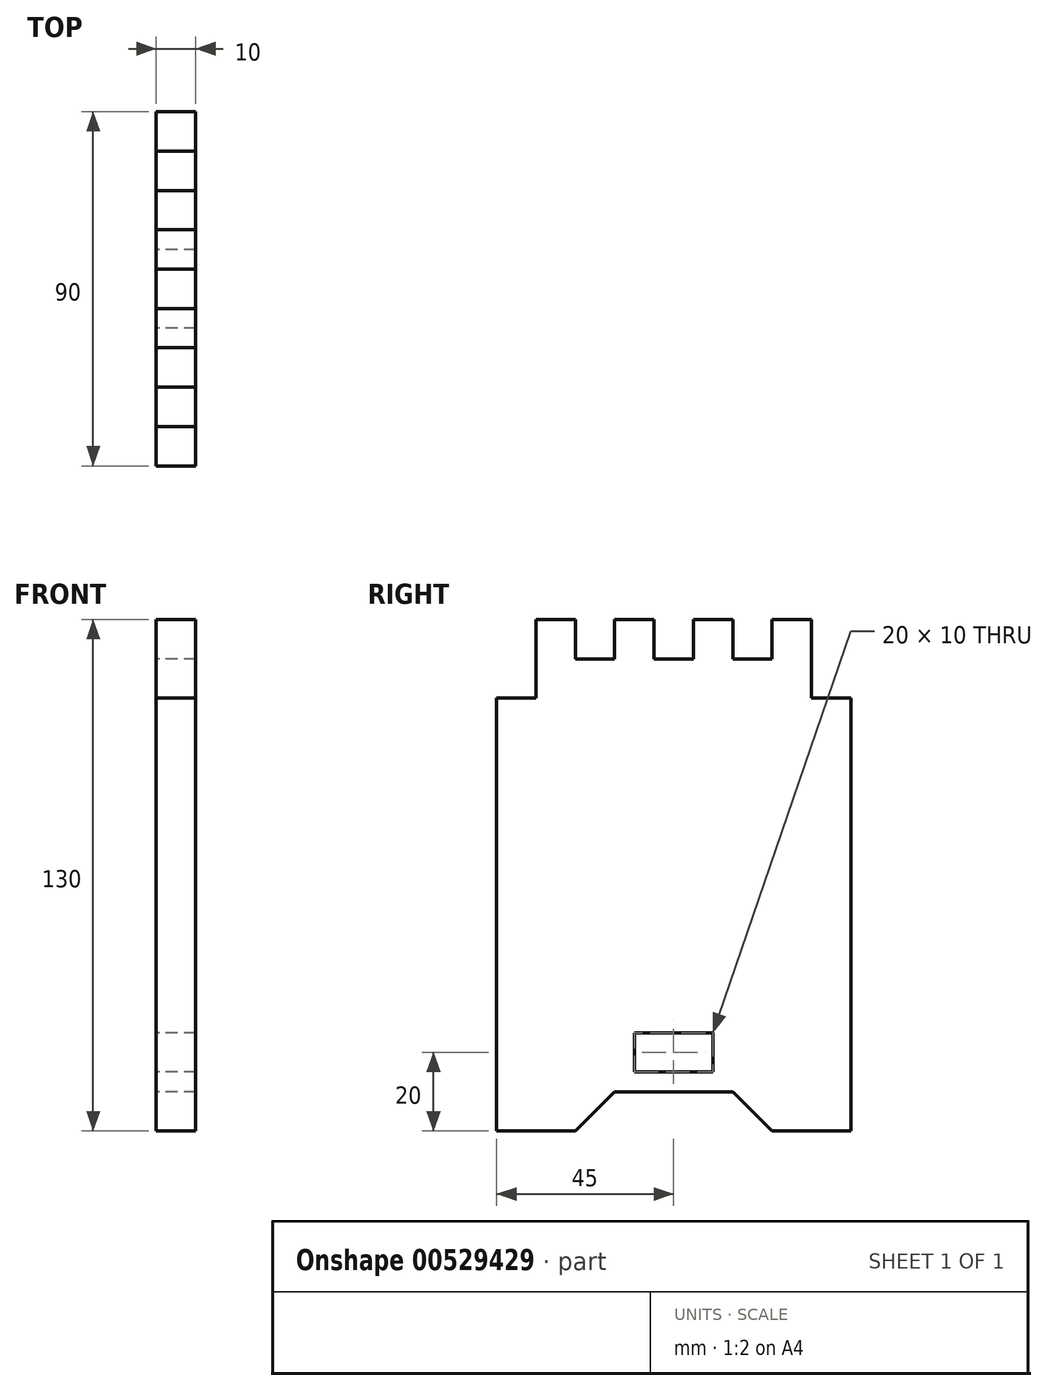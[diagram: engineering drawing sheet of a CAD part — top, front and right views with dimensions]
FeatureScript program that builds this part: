
annotation { "Feature Type Name" : "Feature", "Feature Type Description" : "" }
export const myFeature = defineFeature(function(context is Context, id is Id, definition is map)
    precondition{}
    {
        {
            var Q0;
            Q0=qCreatedBy(makeId("Right.planeOp"),FACE);
            var sketch = newSketch(context, id + "F0", { "sketchPlane" : qUnion([Q0])});
            skLineSegment(sketch, "E0.left", {"start": v(45, -65) * mm, "end": v(45, 45) * mm});
            skLineSegment(sketch, "E0.right", {"start": v(-45, -65) * mm, "end": v(-45, 45) * mm});
            skPoint(sketch, "E0.middle", {"position": v(0, 0) * mm});
            skLineSegment(sketch, "E1", {"start": v(45, -65) * mm, "end": v(25, -65) * mm});
            skLineSegment(sketch, "E2", {"start": v(25, -65) * mm, "end": v(15, -55) * mm});
            skLineSegment(sketch, "E3.MirrorCS", {"start": v(-25, -65) * mm, "end": v(-15, -55) * mm});
            skLineSegment(sketch, "E4.MirrorCS", {"start": v(-45, -65) * mm, "end": v(-25, -65) * mm});
            skLineSegment(sketch, "E5", {"start": v(-15, -55) * mm, "end": v(15, -55) * mm});
            skLineSegment(sketch, "E6", {"start": v(-35, 65) * mm, "end": v(-25, 65) * mm});
            skLineSegment(sketch, "E7", {"start": v(-25, 65) * mm, "end": v(-25, 55) * mm});
            skLineSegment(sketch, "E8", {"start": v(-25, 55) * mm, "end": v(-15, 55) * mm});
            skLineSegment(sketch, "E9", {"start": v(-15, 55) * mm, "end": v(-15, 65) * mm});
            skLineSegment(sketch, "E10", {"start": v(-15, 65) * mm, "end": v(-5.01, 65) * mm});
            skLineSegment(sketch, "E11", {"start": v(-5.01, 65) * mm, "end": v(-5.01, 55) * mm});
            skLineSegment(sketch, "E12", {"start": v(-5.01, 55) * mm, "end": v(4.99, 55) * mm});
            skLineSegment(sketch, "E13", {"start": v(4.99, 55) * mm, "end": v(4.99, 65) * mm});
            skLineSegment(sketch, "E14", {"start": v(4.99, 65) * mm, "end": v(15, 65) * mm});
            skLineSegment(sketch, "E15", {"start": v(15, 65) * mm, "end": v(15, 55) * mm});
            skLineSegment(sketch, "E16", {"start": v(15, 55) * mm, "end": v(25, 55) * mm});
            skLineSegment(sketch, "E17", {"start": v(25, 55) * mm, "end": v(25, 65) * mm});
            skLineSegment(sketch, "E18", {"start": v(25, 65) * mm, "end": v(35, 65) * mm});
            skPoint(sketch, "E19", {"position": v(0, -45) * mm});
            skLineSegment(sketch, "E20.bottom", {"start": v(10, -50) * mm, "end": v(-10, -50) * mm});
            skLineSegment(sketch, "E20.top", {"start": v(10, -40) * mm, "end": v(-10, -40) * mm});
            skLineSegment(sketch, "E20.left", {"start": v(10, -50) * mm, "end": v(10, -40) * mm});
            skLineSegment(sketch, "E20.right", {"start": v(-10, -50) * mm, "end": v(-10, -40) * mm});
            skLineSegment(sketch, "E21", {"start": v(-35, 65) * mm, "end": v(-35, 45) * mm});
            skLineSegment(sketch, "E22", {"start": v(-35, 45) * mm, "end": v(-45, 45) * mm});
            skLineSegment(sketch, "E23", {"start": v(35, 45) * mm, "end": v(45, 45) * mm});
            skLineSegment(sketch, "E24", {"start": v(35, 65) * mm, "end": v(35, 45) * mm});
            skSolve(sketch);
        }
        {
            var Q0;
            Q0=makeQuery(id+"F0.imprint","IMPRINT",FACE,{"disambiguationData":[TD([[makeQuery(id+"F0.imprint","IMPRINT",EDGE,{"derivedFrom":sQuery(id+"F0.wireOp",EDGE,"E0.left")}),1.0]])]});
            extrude(context, id + "F1", {"entities" : qUnion([Q0]), "depth" : 10 * mm, "offsetDistance" : 25 * mm});
        }
    });
